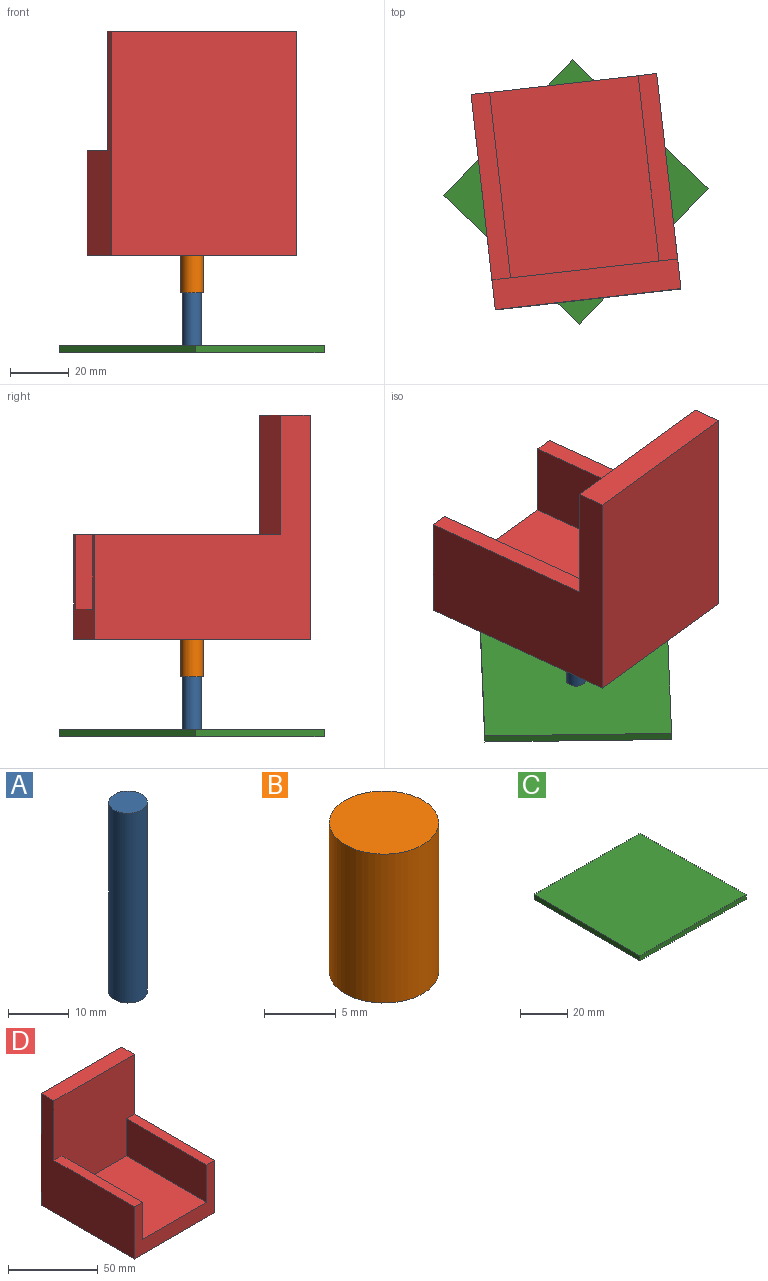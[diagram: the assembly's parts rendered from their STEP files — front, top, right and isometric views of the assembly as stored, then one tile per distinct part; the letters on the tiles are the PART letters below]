
ASSEMBLY  parts=4 mates=3
PART A: 3 faces, bbox 6.4x6.4x38.1 mm
  f0: cylinder r=3.17mm len=38.1mm, axis (0,0,1), area 760.1mm2, adj f1,f2
  f1: plane 6.35x6.35mm, normal (0,0,-1), area 31.7mm2, adj f0
  f2: plane 6.35x6.35mm, normal (0,0,1), area 31.7mm2, adj f0
PART B: 3 faces, bbox 7.6x7.6x12.7 mm
  f0: cylinder r=3.81mm len=12.7mm, axis (0,0,1), area 304mm2, adj f1,f2
  f1: plane 7.62x7.62mm, normal (0,0,-1), area 45.6mm2, adj f0
  f2: plane 7.62x7.62mm, normal (0,0,1), area 45.6mm2, adj f0
PART C: 6 faces, bbox 63.5x63.5x2.5 mm
  f0: plane 63.5x2.54mm, normal (0,1,0), area 161.3mm2, adj f1,f3,f4,f5
  f1: plane 63.5x2.54mm, normal (1,0,0), area 161.3mm2, adj f0,f2,f4,f5
  f2: plane 63.5x2.54mm, normal (0,-1,0), area 161.3mm2, adj f1,f3,f4,f5
  f3: plane 63.5x2.54mm, normal (-1,0,0), area 161.3mm2, adj f0,f2,f4,f5
  f4: plane 63.5x63.5mm, normal (0,0,-1), area 4032.3mm2, adj f0,f1,f2,f3
  f5: plane 63.5x63.5mm, normal (0,0,1), area 4032.3mm2, adj f0,f1,f2,f3
PART D: 12 faces, bbox 63.5x73.7x76.2 mm
  f0: plane 66.04x63.5mm, normal (0,-1,0), area 3871mm2, adj f1,f3,f4,f6,f8,f9,f10,f11
  f1: plane 63.5x50.8mm, normal (0,0,1), area 3225.8mm2, adj f0,f2,f9,f11
  f2: plane 63.5x35.56mm, normal (0,-1,0), area 967.7mm2, adj f1,f3,f4,f5,f8,f9,f10,f11
  f3: plane 76.2x73.66mm, normal (1,0,0), area 3032.3mm2, adj f0,f2,f5,f6,f7,f10
  f4: plane 76.2x73.66mm, normal (-1,0,0), area 3032.3mm2, adj f0,f2,f5,f6,f7,f8
  f5: plane 73.66x63.5mm, normal (0,0,-1), area 4677.4mm2, adj f2,f3,f4,f7
  f6: plane 63.5x10.16mm, normal (0,0,1), area 645.2mm2, adj f0,f3,f4,f7
  f7: plane 76.2x63.5mm, normal (0,1,0), area 4838.7mm2, adj f3,f4,f5,f6
  f8: plane 63.5x6.35mm, normal (0,0,1), area 403.2mm2, adj f0,f2,f4,f9
  f9: plane 63.5x25.4mm, normal (1,0,0), area 1612.9mm2, adj f0,f1,f2,f8
  f10: plane 63.5x6.35mm, normal (0,0,1), area 403.2mm2, adj f0,f2,f3,f11
  f11: plane 63.5x25.4mm, normal (-1,0,0), area 1612.9mm2, adj f0,f1,f2,f10
PLACE A rot(axis=(0,0,-1),43.7deg) t=(25.58,66.37,40.75)mm
PLACE B rot(axis=(0,0,-1),43.7deg) t=(25.58,66.37,20.64)mm
PLACE C rot(axis=(0,0,-1),43.7deg) t=(25.58,66.37,40.75)mm fixed
PLACE D rot(axis=(0,0,-1),173.6deg) t=(25.01,71.42,20.64)mm
MATE fastened C.f5 <-> A.f0  axis (0,0,1) through (25.58,66.37,-10.05)mm
MATE slider A.f0 <-> B.f0  axis (0,0,1) through (25.58,66.37,28.05)mm
MATE revolute D.f5 <-> B.f0  axis (0,0,-1) through (25.58,66.37,20.64)mm
